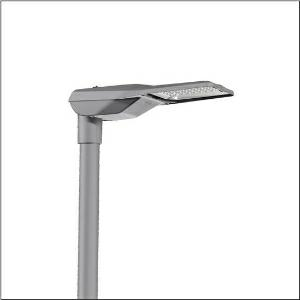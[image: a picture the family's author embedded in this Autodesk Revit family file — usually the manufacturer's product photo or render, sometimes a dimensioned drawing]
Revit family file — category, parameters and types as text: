
# Revit family: streetlight_sl_21_mini___st1_5a_5xe2p43s08hb_a927
name_source: partatom
category: Lighting Fixtures
units: mm (PartAtom-declared; Revit-internal decimal feet)

## family parameters
Cut with Voids When Loaded = No
Host = Face
Light Source = No
Part Type = Normal
Room Calculation Point = No
Round Connector Dimension = Use Diameter
Shared = No

## types (1)
- --- (1 x LED, 9260 lm, 66 W, 4000K)
    Apparent Load = 66 VA
    CIE Flux Codes = 22 53 95 100 100
    Color Rendering = 70
    Color Temperature = 4000K
    Default Elevation = 1800 mm
    Description = Streetlight SL 21 mini, mast luminaire, primary light control with lens, of PMMA, primary optical cover: cover, of toughened safety glass, transparent, light distribution: ST1.5a, light emission: direct distribution, primary light characteristic: asymmetric, installation type: side-entry, post-top, LED, High Power LED, rated luminous flux: 9.260lm, luminous efficacy: 140lm/W, light colour: 740, colour temperature: 4000K, control gear: D4i, control: overheat protection, constant luminous flux control, time-dependent luminous flux control, flexible luminous flux parameterisation, pre-setting: logarithmic dimming characteristic, mains connection: 220..240V, AC, 50/60Hz, start of lifetime: 66W, end of service life: 69W, reduction: 30W, luminaire housing, of diecast aluminium, powder-coated, Siteco® metallic grey (DB 702S), corrosivity category C5 mid according to DIN EN ISO 12944, please order mast flange separately, inclination adjustable: 0°, 5°, 10°, 15°, sealing non-destructively replaceable, multi-level sealing system, length: 628mm, width: 235mm, height: 110mm, mast flange for spigot size: 42mm (side-entry): 5XC10008XM4, 60/48mm (side-entry/post-top): 5XC10108XM2, 76/60mm (side-entry/post-top): 5XC10108XM1, mounting height: 4..8m, Smart Interface above, protection rating (complete): IP66, insulation class (complete): insulation class II (safety insulation), certification: CE, ENEC, ENEC+, VDE, impact resistance: IK10, permissible operating ambient temperature for outdoor applications: -40..+50°C, standard-compliant lighting for roads and squares, packaging unit: 1 piece

Light Distribution: ST1.5a
    Height = 110 mm
    Lamp = 1 x LED
    Lamp Light Flux = 9260 lm
    Lamp Power = 66 W
    Lamp count = 1
    Length = 625 mm
    Luminous efficacy = 140 lm/W
    Manufacturer = Siteco
    ModVariant = No
    Model = 5XE2P43S08HB
    Number of Poles = 1
    OnlyDefault = Yes
    Power Factor = 1
    Product Name = Streetlight SL 21 mini | ST1.5a
    Product group = mast luminaire | pylon top
    ProductGroupID = 6100
    Protection Class = Protection class II
    Protection Degree = IP 66
    RLX_Detail_Level = 1
    RLX_Emergency_Light_Flux = 0 lm
    RLX_Emergency_Type = 0
    RLX_Emergency_Type_DB = No
    RlxData = <blob elided: 29633 chars, md5=6ccf8d83>
    Socket = socket
    Standby Power = 0 W
    System Light Flux = 9260 lm
    System Power = 66 W
    Type Comments = factory setting: luminous flux: 100 % | dim-lin: 254 | 670 mA
    Type Image = l_1003515.jpg
    URL = http://relux.com
    VarID = @adj_197077
    Voltage = 0 V
    Weight = 0.00 kg
    Width = 234 mm

## geometry (parser evidence)
native form markers: Blend x4, Sweep x8
no freeform markers — native parametric forms only
